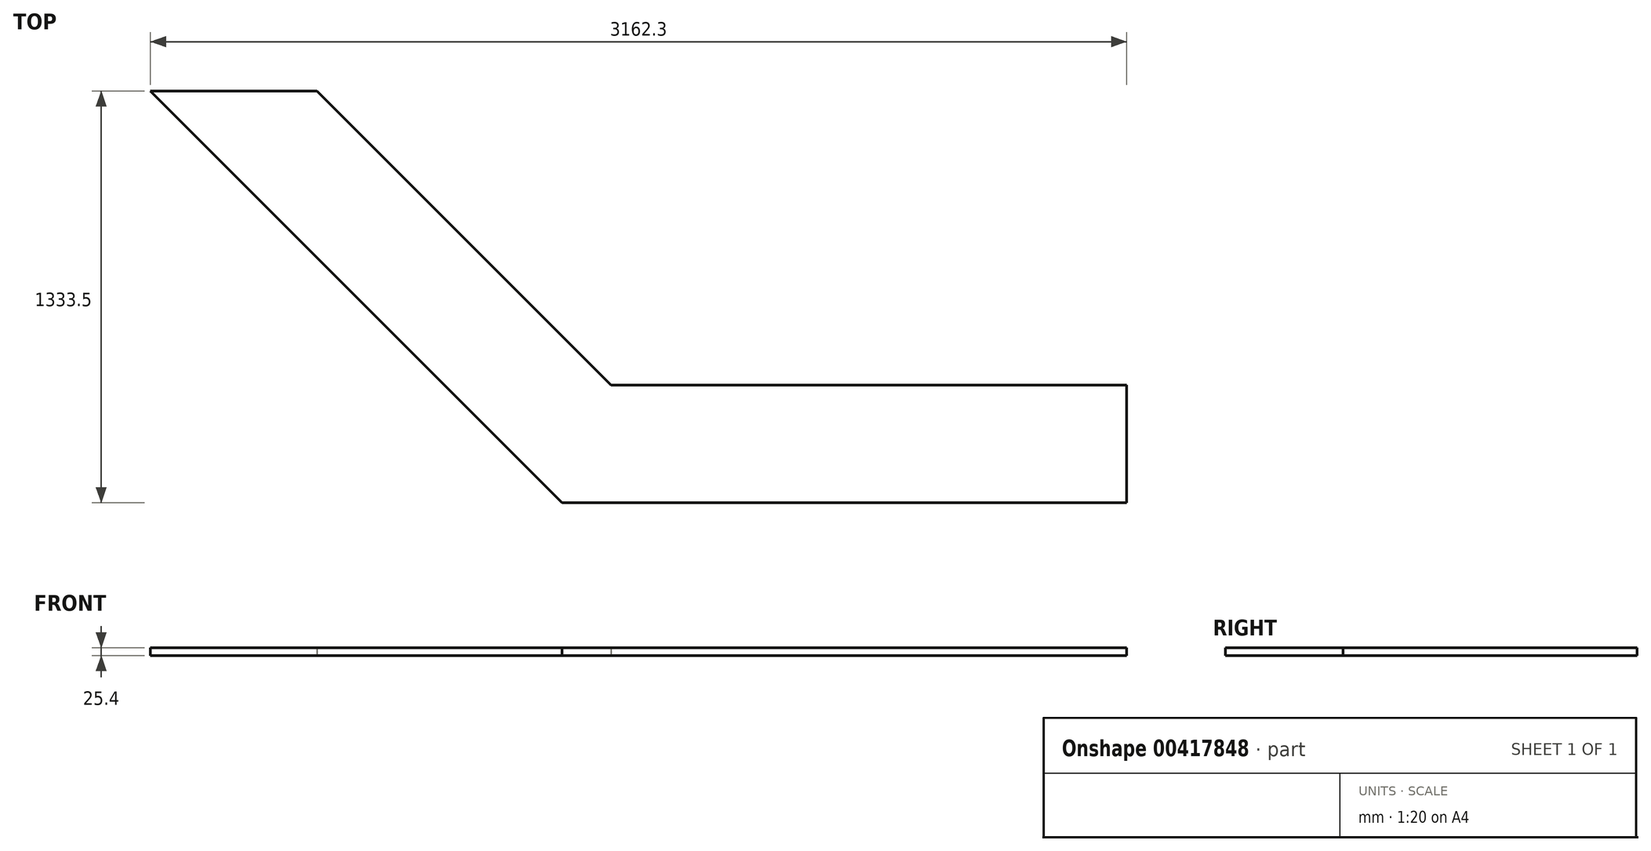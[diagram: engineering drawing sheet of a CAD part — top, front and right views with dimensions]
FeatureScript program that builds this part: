
annotation { "Feature Type Name" : "Feature", "Feature Type Description" : "" }
export const myFeature = defineFeature(function(context is Context, id is Id, definition is map)
    precondition{}
    {
        {
            var Q0;
            Q0=qCreatedBy(makeId("Top.planeOp"),FACE);
            var sketch = newSketch(context, id + "F0", { "sketchPlane" : qUnion([Q0])});
            skLineSegment(sketch, "E0", {"start": v(0, 0) * mm, "end": v(-1828.8, 0) * mm});
            skLineSegment(sketch, "E1", {"start": v(-1828.8, 0) * mm, "end": v(-3162.3, 1333.5) * mm});
            skLineSegment(sketch, "E2", {"start": v(-3162.3, 1333.5) * mm, "end": v(-2623.48, 1333.5) * mm});
            skLineSegment(sketch, "E3", {"start": v(-2623.48, 1333.5) * mm, "end": v(-1670.98, 381) * mm});
            skLineSegment(sketch, "E4", {"start": v(-1670.98, 381) * mm, "end": v(0, 381) * mm});
            skLineSegment(sketch, "E5", {"start": v(0, 381) * mm, "end": v(0, 0) * mm});
            skLineSegment(sketch, "E6", {"start": v(-2147.23, 857.25) * mm, "end": v(-2416.64, 587.84) * mm, "construction": true});
            skSolve(sketch);
        }
        {
            var Q0;
            Q0=qSketchRegion(id+"F0",true);
            extrude(context, id + "F1", {"entities" : qUnion([Q0]), "depth" : 25.4 * mm});
        }
    });
